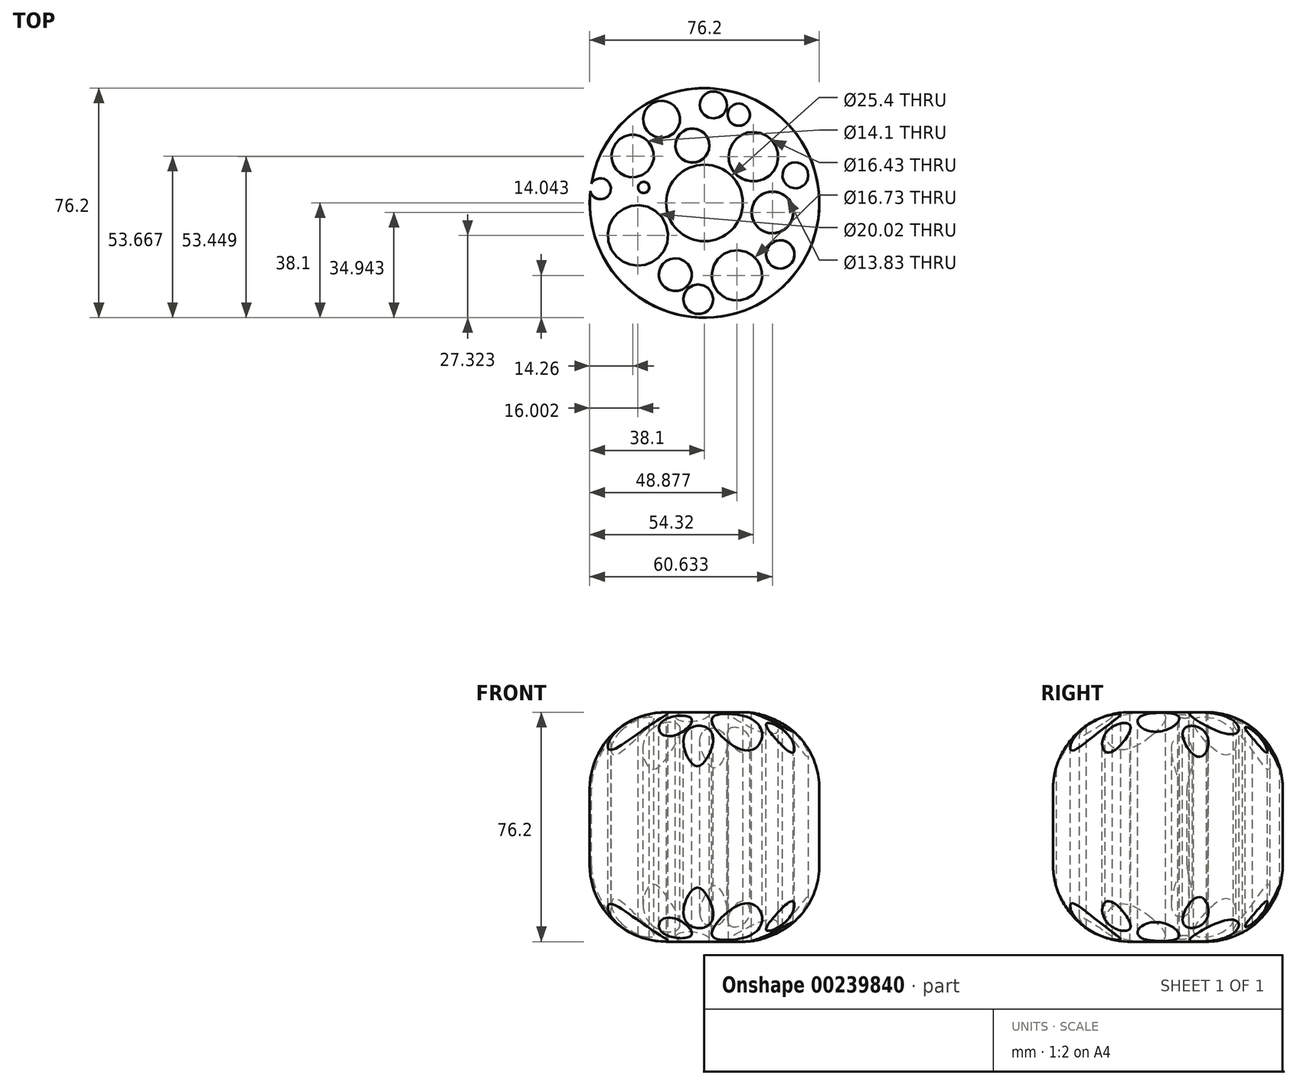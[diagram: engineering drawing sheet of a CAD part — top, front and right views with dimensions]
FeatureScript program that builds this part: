
annotation { "Feature Type Name" : "Feature", "Feature Type Description" : "" }
export const myFeature = defineFeature(function(context is Context, id is Id, definition is map)
    precondition{}
    {
        {
            var Q0;
            Q0=qCreatedBy(makeId("Top.planeOp"),FACE);
            var sketch = newSketch(context, id + "F0", { "sketchPlane" : qUnion([Q0])});
            skCircle(sketch, "E0", {"center": v(0, 0) * mm, "radius": 38.1 * mm});
            skSolve(sketch);
        }
        {
            var Q0;
            Q0=makeQuery(id+"F0.imprint","IMPRINT",FACE,{"disambiguationData":[TD([[makeQuery(id+"F0.imprint","IMPRINT",EDGE,{"derivedFrom":sQuery(id+"F0.wireOp",EDGE,"E0")}),1.0]])]});
            extrude(context, id + "F1", {"entities" : qUnion([Q0]), "oppositeDirection" : true, "depth" : 76.2 * mm});
        }
        {
            var Q0;
            Q0=makeQuery(id+"F1.opExtrude","CAP_FACE",FACE,{"disambiguationData":[OSD([sQuery(id+"F0.wireOp",EDGE,"E0")])],"isStart":false});
            var sketch = newSketch(context, id + "F2", { "sketchPlane" : qUnion([Q0])});
            skCircle(sketch, "E1", {"center": v(0, 0) * mm, "radius": 12.7 * mm});
            skSolve(sketch);
        }
        {
            var Q0;
            Q0 = qSketchRegion(id + "F2", true);
            extrude(context, id + "F3", {"entities" : qUnion([Q0]), "operationType" : NewBodyOperationType.REMOVE, "oppositeDirection" : true, "depth" : 180.85 * mm});
        }
        {
            var Q0;
            Q0=qCreatedBy(makeId("Top.planeOp"),FACE);
            var sketch = newSketch(context, id + "F4", { "sketchPlane" : qUnion([Q0])});
            skCircle(sketch, "E2", {"center": v(-23.84, 15.57) * mm, "radius": 7.05 * mm});
            skCircle(sketch, "E3", {"center": v(-22.1, -10.78) * mm, "radius": 10 * mm});
            skCircle(sketch, "E4", {"center": v(10.78, -24.06) * mm, "radius": 8.36 * mm});
            skCircle(sketch, "E5", {"center": v(-9.69, -23.84) * mm, "radius": 5.46 * mm});
            skCircle(sketch, "E6", {"center": v(16.22, 15.35) * mm, "radius": 8.22 * mm});
            skCircle(sketch, "E7", {"center": v(22.53, -3.16) * mm, "radius": 6.92 * mm});
            skCircle(sketch, "E8", {"center": v(25.15, -17.1) * mm, "radius": 4.7 * mm});
            skCircle(sketch, "E9", {"center": v(-14.26, 27.76) * mm, "radius": 6.11 * mm});
            skCircle(sketch, "E10", {"center": v(-4.03, 19.05) * mm, "radius": 5.66 * mm});
            skCircle(sketch, "E11", {"center": v(2.94, 32.55) * mm, "radius": 4.49 * mm});
            skCircle(sketch, "E12", {"center": v(-34.5, 4.7) * mm, "radius": 3.47 * mm});
            skCircle(sketch, "E13", {"center": v(-20.19, 5.14) * mm, "radius": 1.84 * mm});
            skCircle(sketch, "E14", {"center": v(30.13, 9.17) * mm, "radius": 4.3 * mm});
            skCircle(sketch, "E15", {"center": v(11.35, 29.3) * mm, "radius": 3.69 * mm});
            skCircle(sketch, "E16", {"center": v(-2.07, -31.99) * mm, "radius": 4.93 * mm});
            skSolve(sketch);
        }
        {
            var Q0;
            Q0 = qSketchRegion(id + "F4", true);
            extrude(context, id + "F5", {"entities" : qUnion([Q0]), "operationType" : NewBodyOperationType.REMOVE, "oppositeDirection" : true, "depth" : 128.27 * mm});
        }
        {
            var Q0;
            Q0=makeQuery(id+"F1.opExtrude","CAP_EDGE",EDGE,{"disambiguationData":[OSD([sQuery(id+"F0.wireOp",EDGE,"E0")])],"isStart":false});
            fillet(context, id + "F6", {"entities" : qUnion([Q0]), "radius" : 25.4 * mm, "tangentPropagation" : true, "allowEdgeOverflow" : false});
        }
        {
            var Q0;
            Q0=makeQuery(id+"F1.opExtrude","CAP_EDGE",EDGE,{"disambiguationData":[OSD([sQuery(id+"F0.wireOp",EDGE,"E0")])],"isStart":true});
            fillet(context, id + "F7", {"entities" : qUnion([Q0]), "radius" : 25.4 * mm, "tangentPropagation" : true, "allowEdgeOverflow" : false});
        }
    });
